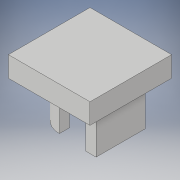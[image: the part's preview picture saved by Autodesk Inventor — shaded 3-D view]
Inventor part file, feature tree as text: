
AUTODESK INVENTOR PART (.ipt)
format: ipt  version: 2019 (Build 230136000, 136)  size: 120,832 bytes
history: native  units: mm
features: extrude x2, sketch x2
ambient origin geometry x8: Origin, YZ Plane, XZ Plane, XY Plane, X Axis, Y Axis, Z Axis, Center Point
bodies: Solid1 (feature_tree)
feature tree (4):
  extrude  "Extrusion1"  Depth=20.0mm
  extrude  "Extrusion2"  Depth=2.5mm
  sketch  "Sketch1"  dims[d0=20.0mm d1=20.0mm]
  sketch  "Sketch2"  dims[d2=5.0mm d3=0.0mm d6=2.5mm d7=2.5mm d9=3.0mm d11=12.0mm d13=2.5mm d14=2.5mm d15=2.5mm d16=10.0mm d17=0.0mm]
